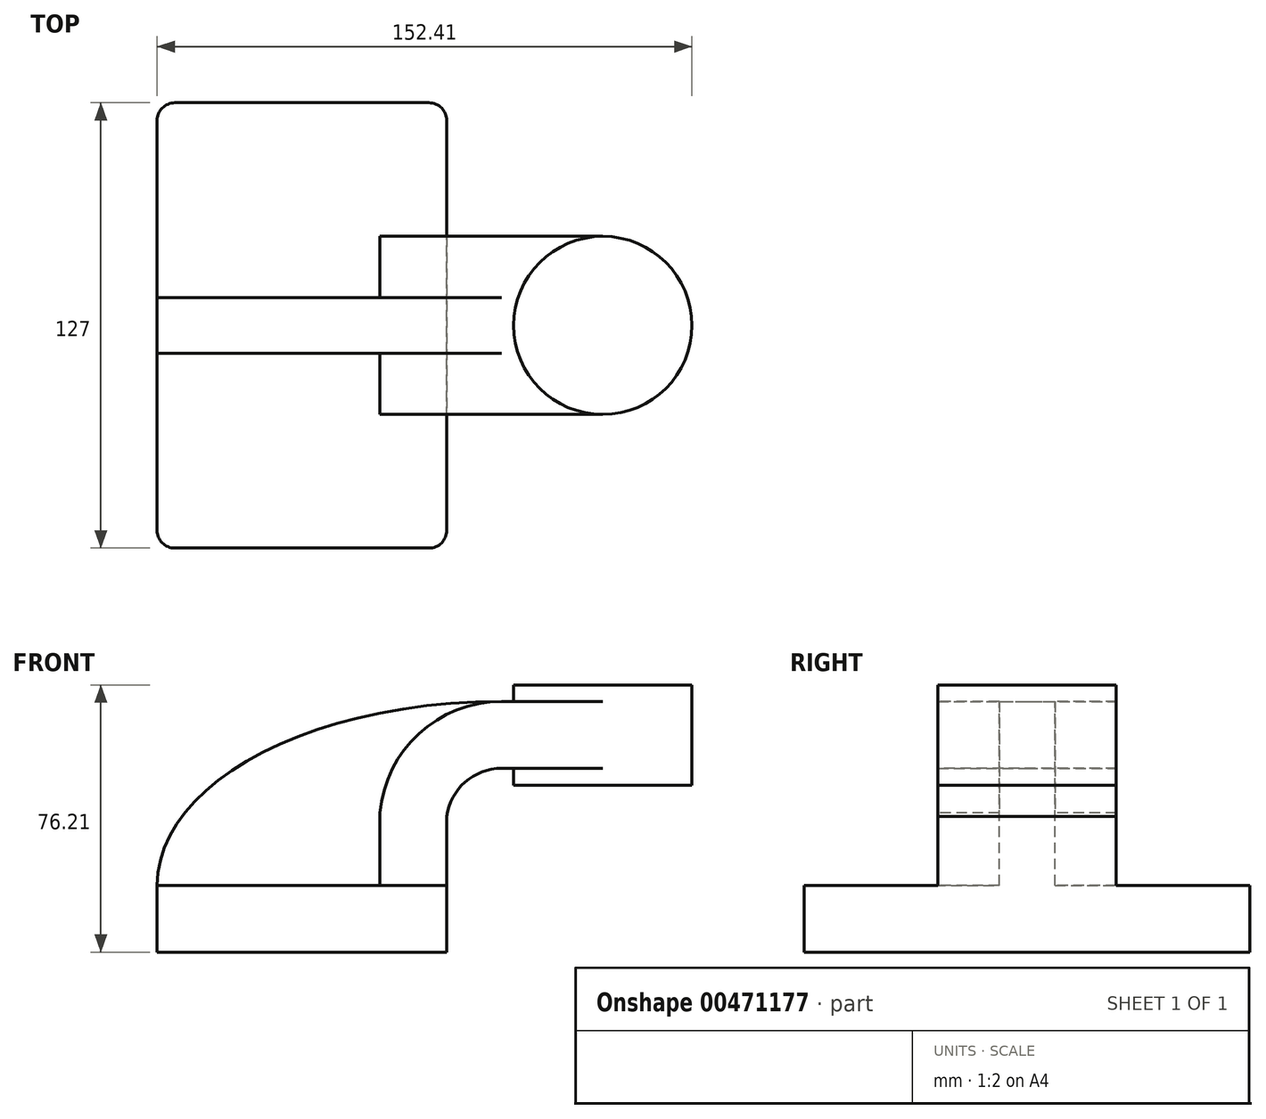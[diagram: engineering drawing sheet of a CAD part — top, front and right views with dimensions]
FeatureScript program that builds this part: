
annotation { "Feature Type Name" : "Feature", "Feature Type Description" : "" }
export const myFeature = defineFeature(function(context is Context, id is Id, definition is map)
    precondition{}
    {
        {
            var Q0;
            Q0=qCreatedBy(makeId("Front.planeOp"),FACE);
            var sketch = newSketch(context, id + "F0", { "sketchPlane" : qUnion([Q0])});
            skLineSegment(sketch, "E0.bottom", {"start": v(-41.28, 9.53) * mm, "end": v(41.28, 9.53) * mm});
            skLineSegment(sketch, "E0.top", {"start": v(-41.28, -9.53) * mm, "end": v(41.28, -9.53) * mm});
            skLineSegment(sketch, "E0.left", {"start": v(-41.28, 9.53) * mm, "end": v(-41.28, -9.53) * mm});
            skLineSegment(sketch, "E0.right", {"start": v(41.28, 9.53) * mm, "end": v(41.28, -9.53) * mm});
            skPoint(sketch, "E0.middle", {"position": v(0, 0) * mm});
            skLineSegment(sketch, "E1.bottom", {"start": v(111.12, 66.68) * mm, "end": v(60.32, 66.68) * mm});
            skLineSegment(sketch, "E1.top", {"start": v(111.12, 38.1) * mm, "end": v(60.32, 38.1) * mm});
            skLineSegment(sketch, "E1.left", {"start": v(111.12, 66.67) * mm, "end": v(111.12, 38.1) * mm});
            skLineSegment(sketch, "E1.right", {"start": v(60.32, 66.68) * mm, "end": v(60.32, 38.1) * mm});
            skPoint(sketch, "E1.middle", {"position": v(85.72, 52.39) * mm});
            skLineSegment(sketch, "E2", {"start": v(41.28, 9.53) * mm, "end": v(41.28, 29.16) * mm});
            skLineSegment(sketch, "E3", {"start": v(56.87, 42.88) * mm, "end": v(85.72, 42.88) * mm});
            skArc(sketch, "E4", {"start": v(56.87, 42.88) * mm, "mid": v(46.49, 38.96) * mm, "end": v(41.28, 29.16) * mm});
            skLineSegment(sketch, "E5.0", {"start": v(56.87, 61.93) * mm, "end": v(85.72, 61.93) * mm});
            skArc(sketch, "E5.1", {"start": v(56.87, 61.93) * mm, "mid": v(33.37, 52.78) * mm, "end": v(22.23, 30.15) * mm});
            skLineSegment(sketch, "E5.2", {"start": v(22.23, 9.53) * mm, "end": v(22.23, 30.15) * mm});
            skLineSegment(sketch, "E6", {"start": v(85.72, 38.1) * mm, "end": v(85.72, 66.68) * mm});
            skFitSpline(sketch, "E7", {"points": [v(-41.28, 9.52) * mm, v(56.87, 61.93) * mm], "startDerivative": vector(0, 83.46) * mm, "endDerivative": vector(170.62, 0) * mm});
            skSolve(sketch);
        }
        {
            var Q0;
            Q0=makeQuery(id+"F0.imprint","IMPRINT",FACE,{"disambiguationData":[TD([[makeQuery(id+"F0.imprint","IMPRINT",EDGE,{"derivedFrom":sQuery(id+"F0.wireOp",EDGE,"E0.top")}),1.0]])]});
            extrude(context, id + "F1", {"entities" : qUnion([Q0]), "endBound" : BoundingType.SYMMETRIC, "depth" : 127 * mm});
        }
        {
            var Q0;
            {var subQ0=sQuery(id+"F0.wireOp",EDGE,"E5.0");var subQ1=sQuery(id+"F0.wireOp",EDGE,"E1.right");var subQ2=makeQuery(id+"F0.imprint","INTERSECT",VERTEX,{"derivedFrom":[subQ1,subQ0]});Q0=makeQuery(id+"F0.imprint","IMPRINT",FACE,{"disambiguationData":[TD([[makeQuery(id+"F0.imprint","IMPRINT",EDGE,{"disambiguationData":[TD([[subQ2,-1.0]])],"derivedFrom":subQ1}),1.0]])]});}
            var Q1;
            {var subQ4=sQuery(id+"F0.wireOp",EDGE,"E2");Q1=makeQuery(id+"F0.imprint","IMPRINT",FACE,{"disambiguationData":[TD([[makeQuery(id+"F0.imprint","IMPRINT",EDGE,{"derivedFrom":subQ4}),1.0]])]});}
            extrude(context, id + "F2", {"entities" : qUnion([Q0, Q1]), "operationType" : NewBodyOperationType.ADD, "endBound" : BoundingType.SYMMETRIC, "oppositeDirection" : true, "depth" : 50.8 * mm});
        }
        {
            var Q0;
            Q0=makeQuery(id+"F0.imprint","IMPRINT",FACE,{"disambiguationData":[TD([[makeQuery(id+"F0.imprint","IMPRINT",EDGE,{"derivedFrom":sQuery(id+"F0.wireOp",EDGE,"E5.1")}),-1.0]])]});
            extrude(context, id + "F3", {"entities" : qUnion([Q0]), "operationType" : NewBodyOperationType.ADD, "endBound" : BoundingType.SYMMETRIC, "depth" : 15.88 * mm});
        }
        {
            var Q0;
            {var subQ4=sQuery(id+"F0.wireOp",EDGE,"E1.left");Q0=makeQuery(id+"F0.imprint","IMPRINT",FACE,{"disambiguationData":[TD([[makeQuery(id+"F0.imprint","IMPRINT",EDGE,{"derivedFrom":subQ4}),-1.0]])]});}
            var Q1;
            {var subQ4=sQuery(id+"F0.wireOp",EDGE,"E1.left");Q1=makeQuery(id+"F0.imprint","IMPRINT",FACE,{"disambiguationData":[TD([[makeQuery(id+"F0.imprint","IMPRINT",EDGE,{"derivedFrom":subQ4}),-1.0]])]});}
            var Q2;
            Q2=sQuery(id+"F0.wireOp",EDGE,"E6");
            revolve(context, id + "F4", {"operationType" : NewBodyOperationType.ADD, "entities" : qUnion([Q0, Q1]), "axis" : qUnion([Q2]), "revolveType" : RevolveType.FULL});
        }
        {
            var Q0;
            Q0=makeQuery(id+"F1.opExtrude","CAP_EDGE",EDGE,{"disambiguationData":[OSD([sQuery(id+"F0.wireOp",EDGE,"E0.left")])],"isStart":false});
            var Q1;
            Q1=makeQuery(id+"F1.opExtrude","CAP_EDGE",EDGE,{"disambiguationData":[OSD([sQuery(id+"F0.wireOp",EDGE,"E0.right")])],"isStart":false});
            var Q2;
            Q2=makeQuery(id+"F1.opExtrude","CAP_EDGE",EDGE,{"disambiguationData":[OSD([sQuery(id+"F0.wireOp",EDGE,"E0.right")])],"isStart":true});
            var Q3;
            Q3=makeQuery(id+"F1.opExtrude","CAP_EDGE",EDGE,{"disambiguationData":[OSD([sQuery(id+"F0.wireOp",EDGE,"E0.left")])],"isStart":true});
            fillet(context, id + "F5", {"entities" : qUnion([Q0, Q1, Q2, Q3]), "radius" : 5.08 * mm, "tangentPropagation" : true, "allowEdgeOverflow" : false});
        }
    });
